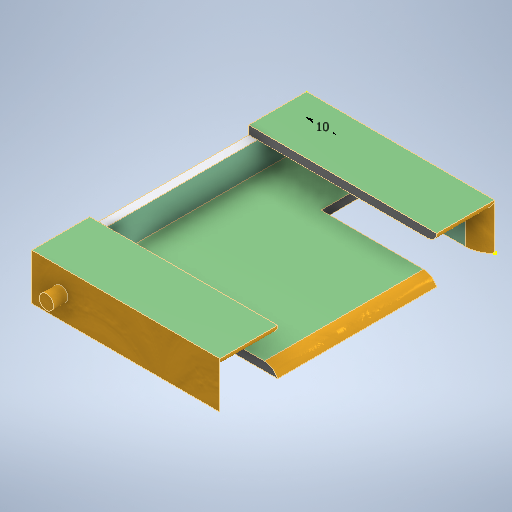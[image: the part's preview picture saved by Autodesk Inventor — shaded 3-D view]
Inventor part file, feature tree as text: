
AUTODESK INVENTOR PART (.ipt)
format: ipt  version: 2025.1 (Build 291241020, 241B)  size: 348,672 bytes
history: native  units: mm
features: extrude x8, sketch x6, fillet x3
ambient origin geometry x8: Origin, YZ Plane, XZ Plane, XY Plane, X Axis, Y Axis, Z Axis, Center Point
bodies: Solid1 (feature_tree)
feature tree (17):
  sketch  "Sketch1"  dims[d0=95.0mm d1=65.0mm]
  extrude  "Extrusion1"  Depth=65.0mm
  extrude  "Extrusion2"  Depth=3.0mm
  extrude  "Extrusion3"  Depth=65.0mm
  extrude  "Extrusion4"  Depth=3.0mm TaperAngle=0.0deg
  extrude  "Extrusion5"  Depth=20.0mm
  extrude  "Extrusion6"  Depth=20.0mm
  extrude  "Extrusion7"  Depth=3.0mm TaperAngle=0.0deg
  fillet  "Fillet1"  [1 undecoded]
  fillet  "Fillet2"  Radius=25.0mm
  fillet  "Fillet3"  Radius=10.0mm
  sketch  "Sketch5"  dims[d13=55.0mm d14=20.0mm]
  sketch  "Sketch6"  dims[d15=20.0mm d16=20.0mm d17=3.0mm d18=0.0mm d22=0.0mm d23=0.0mm d24=25.0mm d25=10.0mm d26=0.0mm d27=10.0mm d28=3.0mm d29=5.0mm d30=5.0mm d31=10.0mm d32=10.0mm d33=5.0mm d34=0.0mm d21=0.5mm d35=0.5mm d36=0.872665mm]
  extrude  "Extrusion8"  Depth=10.0mm
  sketch  "Sketch2"  dims[d2=3.0mm d3=0.0mm d4=3.0mm]
  sketch  "Sketch3"  dims[d5=13.0mm d6=0.0mm d7=65.0mm d8=3.0mm]
  sketch  "Sketch4"  dims[d9=13.0mm d10=0.0mm d11=3.0mm d12=0.0mm]
note: 1 required parameter value undecoded (feature->parameter linkage not recoverable at this tier; creation-order binding heuristic only, values carry confidence <= 0.55)
